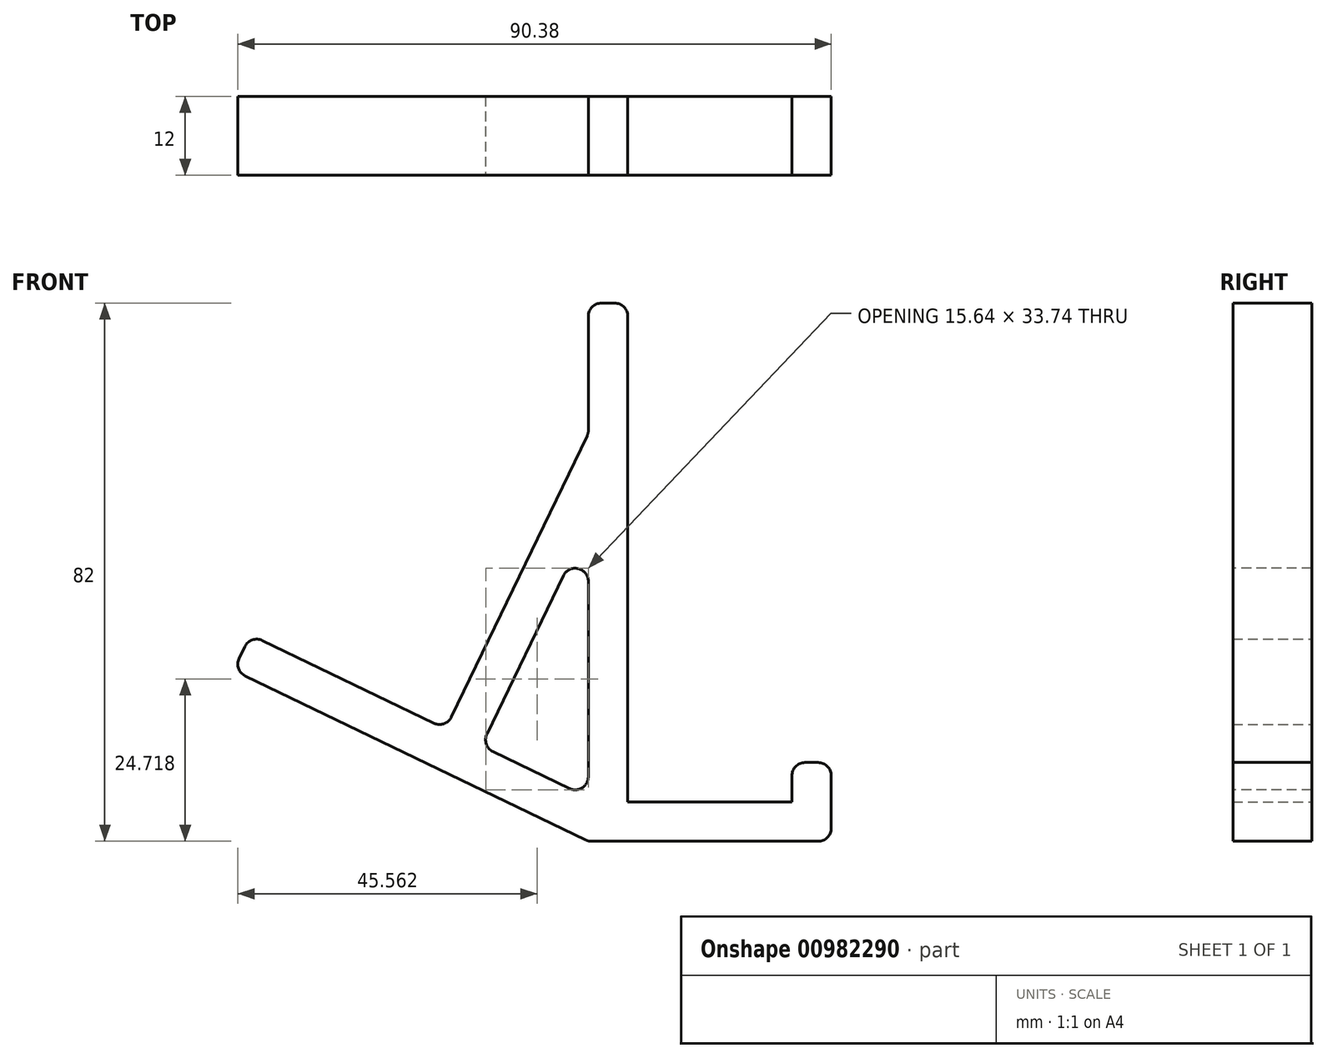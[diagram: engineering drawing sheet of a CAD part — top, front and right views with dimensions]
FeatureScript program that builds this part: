
annotation { "Feature Type Name" : "Feature", "Feature Type Description" : "" }
export const myFeature = defineFeature(function(context is Context, id is Id, definition is map)
    precondition{}
    {
        {
            var Q0;
            Q0=qCreatedBy(makeId("Front.planeOp"),FACE);
            var sketch = newSketch(context, id + "F0", { "sketchPlane" : qUnion([Q0])});
            skLineSegment(sketch, "E0", {"start": v(0, 0) * mm, "end": v(37, 0) * mm});
            skLineSegment(sketch, "E1", {"start": v(37, 0) * mm, "end": v(37, 12) * mm});
            skLineSegment(sketch, "E2", {"start": v(37, 12) * mm, "end": v(31, 12) * mm});
            skLineSegment(sketch, "E3", {"start": v(31, 12) * mm, "end": v(31, 6) * mm});
            skLineSegment(sketch, "E4", {"start": v(31, 6) * mm, "end": v(6, 6) * mm});
            skLineSegment(sketch, "E5", {"start": v(6, 6) * mm, "end": v(6, 82) * mm});
            skLineSegment(sketch, "E6", {"start": v(6, 82) * mm, "end": v(0, 82) * mm});
            skLineSegment(sketch, "E7", {"start": v(0, 82) * mm, "end": v(0, 62.17) * mm});
            skLineSegment(sketch, "E8", {"start": v(0, 0) * mm, "end": v(-54.05, 26.06) * mm});
            skLineSegment(sketch, "E9", {"start": v(-54.05, 26.06) * mm, "end": v(-51.44, 31.46) * mm});
            skLineSegment(sketch, "E10", {"start": v(-51.44, 31.46) * mm, "end": v(-21.71, 17.13) * mm});
            skLineSegment(sketch, "E11", {"start": v(0, 62.17) * mm, "end": v(-21.71, 17.13) * mm});
            skLineSegment(sketch, "E12", {"start": v(0, 82) * mm, "end": v(0, 0) * mm, "construction": true});
            skLineSegment(sketch, "E13", {"start": v(0, 6.66) * mm, "end": v(-16.31, 14.52) * mm});
            skLineSegment(sketch, "E14", {"start": v(-16.31, 14.52) * mm, "end": v(0, 48.35) * mm});
            skLineSegment(sketch, "E15", {"start": v(0, 48.35) * mm, "end": v(0, 6.66) * mm});
            skLineSegment(sketch, "E16", {"start": v(-51.44, 31.46) * mm, "end": v(0, 6.66) * mm, "construction": true});
            skSolve(sketch);
        }
        {
            var Q0;
            Q0 = qSketchRegion(id + "F0", true);
            extrude(context, id + "F1", {"entities" : qUnion([Q0]), "depth" : 12 * mm, "offsetDistance" : 25 * mm});
        }
        {
            var Q0;
            Q0=makeQuery(id+"F1.opExtrude","SWEPT_EDGE",EDGE,{"disambiguationData":[OSD([sQuery(id+"F0.wireOp",EDGE,"E0"),sQuery(id+"F0.wireOp",EDGE,"E1")])]});
            var Q1;
            Q1=makeQuery(id+"F1.opExtrude","SWEPT_EDGE",EDGE,{"disambiguationData":[OSD([sQuery(id+"F0.wireOp",EDGE,"E10"),sQuery(id+"F0.wireOp",EDGE,"E11")])]});
            var Q2;
            Q2=makeQuery(id+"F1.opExtrude","SWEPT_EDGE",EDGE,{"disambiguationData":[OSD([sQuery(id+"F0.wireOp",EDGE,"E7"),sQuery(id+"F0.wireOp",EDGE,"E11")])]});
            var Q3;
            Q3=makeQuery(id+"F1.opExtrude","SWEPT_EDGE",EDGE,{"disambiguationData":[OSD([sQuery(id+"F0.wireOp",EDGE,"E13"),sQuery(id+"F0.wireOp",EDGE,"E14")])]});
            var Q4;
            Q4=makeQuery(id+"F1.opExtrude","SWEPT_EDGE",EDGE,{"disambiguationData":[OSD([sQuery(id+"F0.wireOp",EDGE,"E13"),sQuery(id+"F0.wireOp",EDGE,"E15")])]});
            var Q5;
            Q5=makeQuery(id+"F1.opExtrude","SWEPT_EDGE",EDGE,{"disambiguationData":[OSD([sQuery(id+"F0.wireOp",EDGE,"E2"),sQuery(id+"F0.wireOp",EDGE,"E3")])]});
            var Q6;
            Q6=makeQuery(id+"F1.opExtrude","SWEPT_EDGE",EDGE,{"disambiguationData":[OSD([sQuery(id+"F0.wireOp",EDGE,"E1"),sQuery(id+"F0.wireOp",EDGE,"E2")])]});
            var Q7;
            Q7=makeQuery(id+"F1.opExtrude","SWEPT_EDGE",EDGE,{"disambiguationData":[OSD([sQuery(id+"F0.wireOp",EDGE,"E6"),sQuery(id+"F0.wireOp",EDGE,"E7")])]});
            var Q8;
            Q8=makeQuery(id+"F1.opExtrude","SWEPT_EDGE",EDGE,{"disambiguationData":[OSD([sQuery(id+"F0.wireOp",EDGE,"E5"),sQuery(id+"F0.wireOp",EDGE,"E6")])]});
            var Q9;
            Q9=makeQuery(id+"F1.opExtrude","SWEPT_EDGE",EDGE,{"disambiguationData":[OSD([sQuery(id+"F0.wireOp",EDGE,"E9"),sQuery(id+"F0.wireOp",EDGE,"E10")])]});
            var Q10;
            Q10=makeQuery(id+"F1.opExtrude","SWEPT_EDGE",EDGE,{"disambiguationData":[OSD([sQuery(id+"F0.wireOp",EDGE,"E8"),sQuery(id+"F0.wireOp",EDGE,"E9")])]});
            var Q11;
            Q11=makeQuery(id+"F1.opExtrude","SWEPT_EDGE",EDGE,{"disambiguationData":[OSD([sQuery(id+"F0.wireOp",EDGE,"E0"),sQuery(id+"F0.wireOp",EDGE,"E8")])]});
            var Q12;
            Q12=makeQuery(id+"F1.opExtrude","SWEPT_EDGE",EDGE,{"disambiguationData":[OSD([sQuery(id+"F0.wireOp",EDGE,"E14"),sQuery(id+"F0.wireOp",EDGE,"E15")])]});
            fillet(context, id + "F2", {"entities" : qUnion([Q0, Q1, Q2, Q3, Q4, Q5, Q6, Q7, Q8, Q9, Q10, Q11, Q12]), "radius" : 2 * mm, "tangentPropagation" : true, "allowEdgeOverflow" : false});
        }
    });
